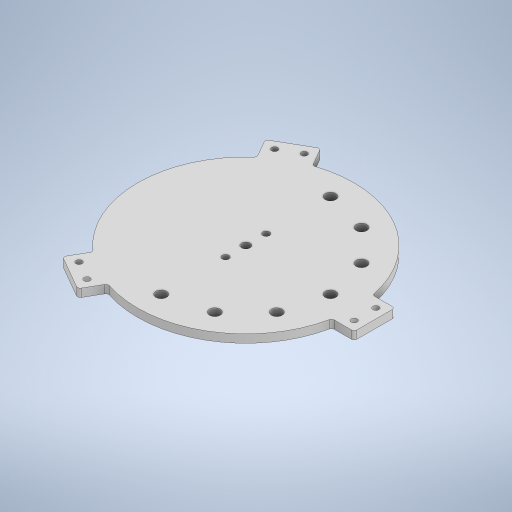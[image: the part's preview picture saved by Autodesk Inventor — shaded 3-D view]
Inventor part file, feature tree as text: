
AUTODESK INVENTOR PART (.ipt)
format: ipt  version: 2023.2 (Build 272271000, 271)  size: 327,168 bytes
history: native  units: in
note: dims shown in document units (in); Inventor stores cm internally (conversion verified against a paired STEP export)
features: sketch x3, extrude x2, hole x1, fillet x1
ambient origin geometry x8: Origin, YZ Plane, XZ Plane, XY Plane, X Axis, Y Axis, Z Axis, Center Point
bodies: Solid1 (feature_tree)
feature tree (7):
  extrude  "Extrusion1"  Depth=0.315in
  hole  "Hole1"  [1 undecoded]
  extrude  "Extrusion2"  Depth=2.4606in
  fillet  "Fillet1"  Radius=3.7402in
  sketch  "Sketch1"  dims[d0=6.2992in d2=0.315in]
  sketch  "Sketch3"  dims[d3=2.7559in d5=180.0deg d7=0.25in]
  sketch  "Sketch4"  dims[d8=0.2362in d9=0.0in d10=2.4606in d12=3.7402in d13=1.1811in d14=1.1811in d16=360.0deg d18=3.1496in d19=0.2756in d20=0.2756in d21=0.2756in d22=1.1811in d24=360.0deg d26=0.1772in d27=0.224in d28=0.3701in d29=0.0787in d30=90.0deg d31=0.315in d32=0.8108in d33=0.1969in d34=0.5906in d35=0.2362in d36=0.0in d37=0.0787in]
note: 1 required parameter value undecoded (feature->parameter linkage not recoverable at this tier; creation-order binding heuristic only, values carry confidence <= 0.55)
